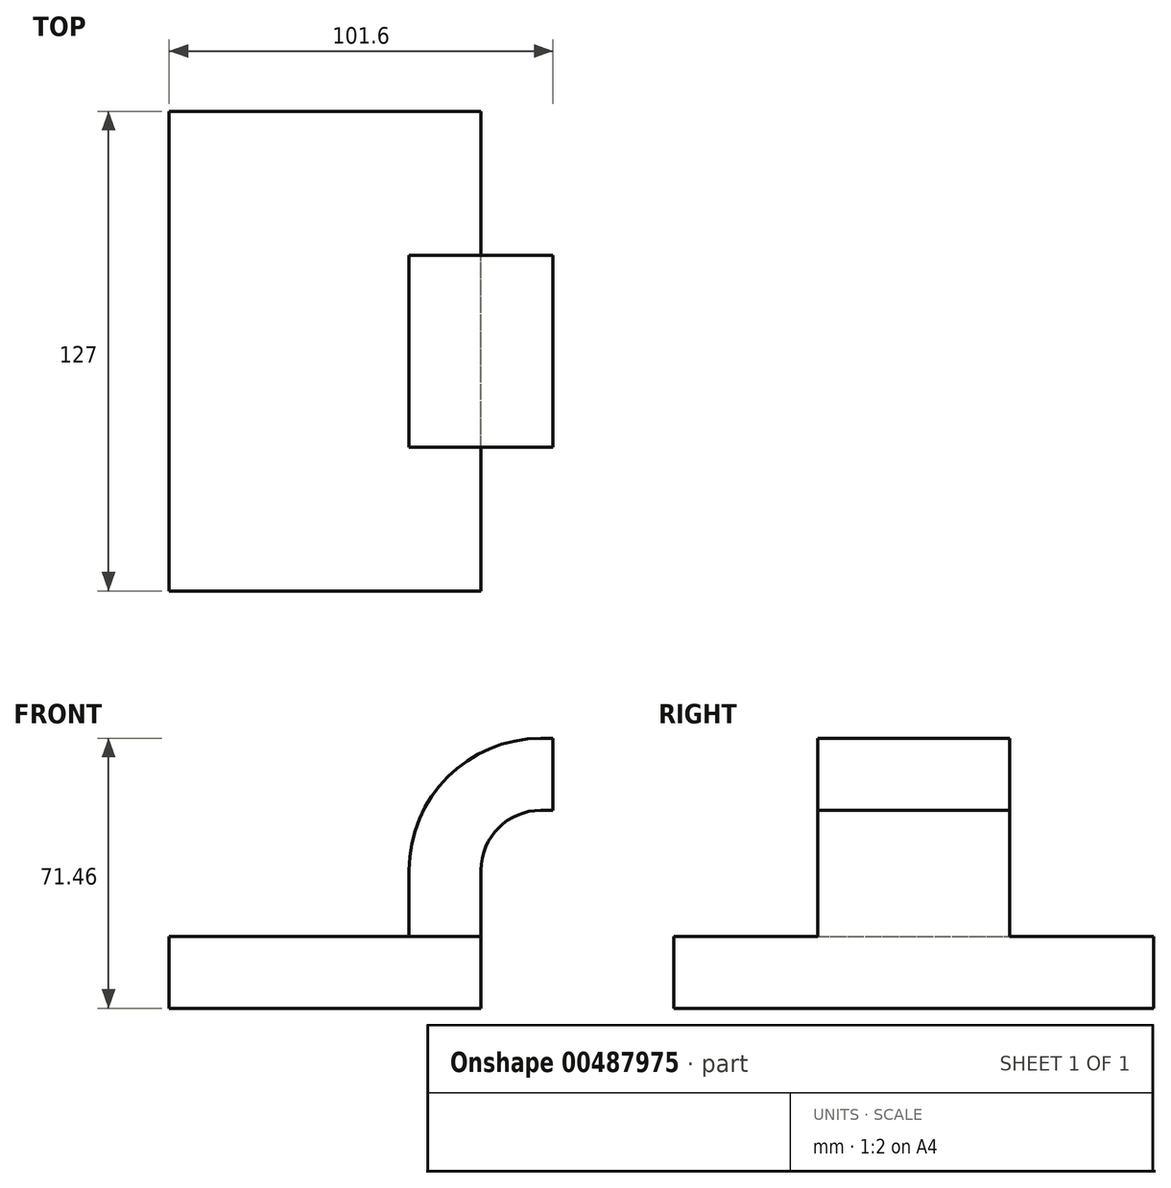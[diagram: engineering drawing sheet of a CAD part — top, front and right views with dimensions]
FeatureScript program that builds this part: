
annotation { "Feature Type Name" : "Feature", "Feature Type Description" : "" }
export const myFeature = defineFeature(function(context is Context, id is Id, definition is map)
    precondition{}
    {
        {
            var Q0;
            Q0=qCreatedBy(makeId("Front.planeOp"),FACE);
            var sketch = newSketch(context, id + "F0", { "sketchPlane" : qUnion([Q0])});
            skLineSegment(sketch, "E0.bottom", {"start": v(41.27, -9.52) * mm, "end": v(-41.27, -9.53) * mm});
            skLineSegment(sketch, "E0.top", {"start": v(41.27, 9.53) * mm, "end": v(-41.28, 9.53) * mm});
            skLineSegment(sketch, "E0.left", {"start": v(41.27, -9.52) * mm, "end": v(41.27, 9.53) * mm});
            skLineSegment(sketch, "E0.right", {"start": v(-41.28, -9.53) * mm, "end": v(-41.28, 9.53) * mm});
            skPoint(sketch, "E0.middle", {"position": v(0, 0) * mm});
            skLineSegment(sketch, "E1.bottom", {"start": v(111.12, 66.68) * mm, "end": v(60.32, 66.68) * mm});
            skLineSegment(sketch, "E1.top", {"start": v(111.12, 38.1) * mm, "end": v(60.32, 38.1) * mm});
            skLineSegment(sketch, "E1.left", {"start": v(111.12, 66.68) * mm, "end": v(111.12, 38.1) * mm});
            skLineSegment(sketch, "E1.right", {"start": v(60.32, 66.68) * mm, "end": v(60.32, 38.1) * mm});
            skPoint(sketch, "E1.middle", {"position": v(85.72, 52.39) * mm});
            skLineSegment(sketch, "E2", {"start": v(41.27, 9.53) * mm, "end": v(41.27, 27) * mm});
            skArc(sketch, "E3", {"start": v(41.27, 27) * mm, "mid": v(45.92, 38.23) * mm, "end": v(57.15, 42.88) * mm});
            skLineSegment(sketch, "E4", {"start": v(57.15, 42.88) * mm, "end": v(85.72, 42.88) * mm});
            skLineSegment(sketch, "E5.0", {"start": v(57.15, 61.93) * mm, "end": v(85.72, 61.93) * mm});
            skArc(sketch, "E5.1", {"start": v(22.22, 27) * mm, "mid": v(32.45, 51.7) * mm, "end": v(57.15, 61.93) * mm});
            skLineSegment(sketch, "E5.2", {"start": v(22.23, 9.53) * mm, "end": v(22.23, 27) * mm});
            skLineSegment(sketch, "E6", {"start": v(85.72, 42.88) * mm, "end": v(85.72, 66.68) * mm});
            skFitSpline(sketch, "E7", {"points": [v(-41.28, 9.53) * mm, v(60.32, 66.67) * mm], "startDerivative": vector(43.82, 109.84) * mm, "endDerivative": vector(126, 12.84) * mm});
            skLineSegment(sketch, "E8", {"start": v(85.72, 66.68) * mm, "end": v(85.72, 38.1) * mm});
            skSolve(sketch);
        }
        {
            var Q0;
            Q0=makeQuery(id+"F0.imprint","IMPRINT",FACE,{"disambiguationData":[TD([[makeQuery(id+"F0.imprint","IMPRINT",EDGE,{"derivedFrom":sQuery(id+"F0.wireOp",EDGE,"E0.bottom")}),-1.0]])]});
            extrude(context, id + "F1", {"entities" : qUnion([Q0]), "endBound" : BoundingType.SYMMETRIC, "depth" : 127 * mm});
        }
        {
            var Q0;
            {var subQ1=sQuery(id+"F0.wireOp",EDGE,"E2");Q0=makeQuery(id+"F0.imprint","IMPRINT",FACE,{"disambiguationData":[TD([[makeQuery(id+"F0.imprint","IMPRINT",EDGE,{"derivedFrom":subQ1}),1.0]])]});}
            extrude(context, id + "F2", {"entities" : qUnion([Q0]), "operationType" : NewBodyOperationType.ADD, "endBound" : BoundingType.SYMMETRIC, "depth" : 50.8 * mm});
        }
        {
            var Q0;
            {var subQ0=sQuery(id+"F0.wireOp",EDGE,"E5.1");Q0=makeQuery(id+"F0.imprint","IMPRINT",FACE,{"disambiguationData":[TD([[makeQuery(id+"F0.imprint","IMPRINT",EDGE,{"derivedFrom":subQ0}),1.0]])]});}
            extrude(context, id + "F3", {"entities" : qUnion([Q0]), "operationType" : NewBodyOperationType.ADD, "endBound" : BoundingType.SYMMETRIC, "depth" : 15.88 * mm});
        }
    });
